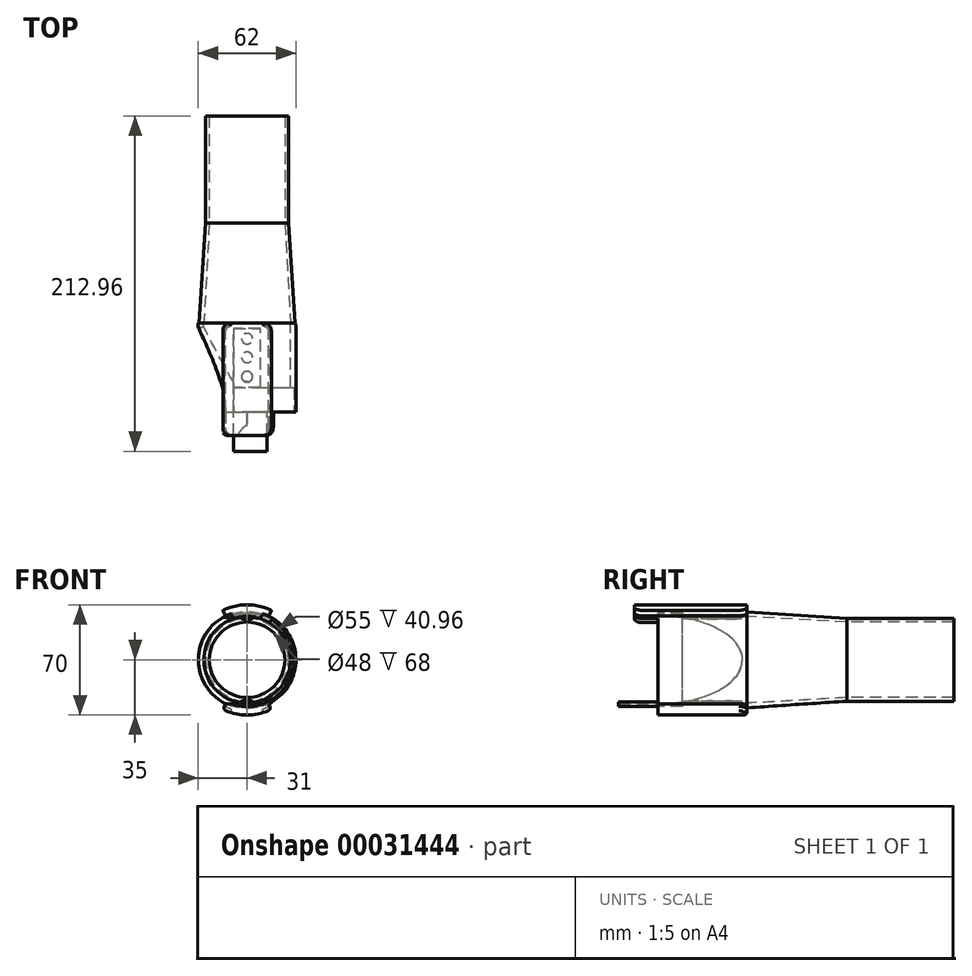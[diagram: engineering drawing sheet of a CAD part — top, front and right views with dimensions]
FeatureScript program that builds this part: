
annotation { "Feature Type Name" : "Feature", "Feature Type Description" : "" }
export const myFeature = defineFeature(function(context is Context, id is Id, definition is map)
    precondition{}
    {
        {
            var Q0;
            Q0=qCreatedBy(makeId("Front.planeOp"),FACE);
            var sketch = newSketch(context, id + "F0", { "sketchPlane" : qUnion([Q0])});
            skCircle(sketch, "E0", {"center": v(0, 0) * mm, "radius": 26.25 * mm});
            skSolve(sketch);
        }
        {
            var Q0;
            Q0=makeQuery(id+"F0.imprint","IMPRINT",FACE,{"disambiguationData":[TD([[makeQuery(id+"F0.imprint","IMPRINT",EDGE,{"derivedFrom":sQuery(id+"F0.wireOp",EDGE,"E0")}),1.0]])]});
            cPlane(context, id + "F1", {"entities" : qUnion([Q0]), "cplaneType" : CPlaneType.OFFSET, "offset" : 63.5 * mm, "width" : 150 * mm, "height" : 150 * mm});
        }
        {
            var Q0;
            Q0=qCreatedBy(id+"F1.planeOp",FACE);
            var sketch = newSketch(context, id + "F2", { "sketchPlane" : qUnion([Q0])});
            skCircle(sketch, "E1.0", {"center": v(0, 0) * mm, "radius": 26.25 * mm, "construction": true});
            skCircle(sketch, "E2", {"center": v(0, 0) * mm, "radius": 30.5 * mm});
            skSolve(sketch);
        }
        {
            var Q0;
            Q0=makeQuery(id+"F0.imprint","IMPRINT",FACE,{"disambiguationData":[TD([[makeQuery(id+"F0.imprint","IMPRINT",EDGE,{"derivedFrom":sQuery(id+"F0.wireOp",EDGE,"E0")}),1.0]])]});
            var Q1;
            Q1=makeQuery(id+"F2.imprint","IMPRINT",FACE,{"disambiguationData":[TD([[makeQuery(id+"F2.imprint","IMPRINT",EDGE,{"derivedFrom":sQuery(id+"F2.wireOp",EDGE,"E2")}),1.0]])]});
            loft(context, id + "F3", {"sheetProfilesArray" : [{ "sheetProfileEntities" : qUnion([Q0]) }, { "sheetProfileEntities" : qUnion([Q1]) }]});
        }
        {
            var Q0;
            Q0=makeQuery(id+"F3.opLoft","CAP_FACE",FACE,{"disambiguationData":[OSD([makeQuery(id+"F2.imprint","IMPRINT",FACE,{"disambiguationData":[TD([[makeQuery(id+"F2.imprint","IMPRINT",EDGE,{"derivedFrom":sQuery(id+"F2.wireOp",EDGE,"E2")}),1.0]])]})])],"isStart":true});
            var sketch = newSketch(context, id + "F4", { "sketchPlane" : qUnion([Q0])});
            skCircle(sketch, "E3.0", {"center": v(0, 0) * mm, "radius": 30.5 * mm, "construction": true});
            skCircle(sketch, "E4.0", {"center": v(0, 0) * mm, "radius": 27.5 * mm});
            skSolve(sketch);
        }
        {
            var Q0;
            Q0=makeQuery(id+"F3.opLoft","CAP_FACE",FACE,{"disambiguationData":[OSD([makeQuery(id+"F0.imprint","IMPRINT",FACE,{"disambiguationData":[TD([[makeQuery(id+"F0.imprint","IMPRINT",EDGE,{"derivedFrom":sQuery(id+"F0.wireOp",EDGE,"E0")}),1.0]])]})])],"isStart":true});
            var sketch = newSketch(context, id + "F5", { "sketchPlane" : qUnion([Q0])});
            skCircle(sketch, "E5.0", {"center": v(0, 0) * mm, "radius": 26.25 * mm, "construction": true});
            skCircle(sketch, "E6", {"center": v(0, 0) * mm, "radius": 24 * mm});
            skSolve(sketch);
        }
        {
            var Q1;
            Q1=makeQuery(id+"F5.imprint","IMPRINT",FACE,{"disambiguationData":[TD([[makeQuery(id+"F5.imprint","IMPRINT",EDGE,{"derivedFrom":sQuery(id+"F5.wireOp",EDGE,"E6")}),1.0]])]});
            var Q2;
            Q2=makeQuery(id+"F4.imprint","IMPRINT",FACE,{"disambiguationData":[TD([[makeQuery(id+"F4.imprint","IMPRINT",EDGE,{"derivedFrom":sQuery(id+"F4.wireOp",EDGE,"E4.0")}),1.0]])]});
            loft(context, id + "F6", {"operationType" : NewBodyOperationType.REMOVE, "sheetProfilesArray" : [{ "sheetProfileEntities" : qUnion([Q1]) }, { "sheetProfileEntities" : qUnion([Q2]) }]});
        }
        {
            var Q0;
            Q0=qCreatedBy(id+"F1.planeOp",FACE);
            var sketch = newSketch(context, id + "F7", { "sketchPlane" : qUnion([Q0])});
            skCircle(sketch, "E7", {"center": v(0, 0) * mm, "radius": 27.5 * mm});
            skCircle(sketch, "E8", {"center": v(0, 0) * mm, "radius": 31 * mm});
            skSolve(sketch);
        }
        {
            var Q0;
            Q0=makeQuery(id+"F7.imprint","IMPRINT",FACE,{"disambiguationData":[TD([[makeQuery(id+"F7.imprint","IMPRINT",EDGE,{"derivedFrom":sQuery(id+"F7.wireOp",EDGE,"E7")}),-1.0]])]});
            extrude(context, id + "F8", {"entities" : qUnion([Q0]), "operationType" : NewBodyOperationType.ADD, "depth" : 56.46 * mm});
        }
        {
            var Q0;
            Q0=makeQuery(id+"F8.opExtrude","CAP_FACE",FACE,{"disambiguationData":[OSD([sQuery(id+"F7.wireOp",EDGE,"E7"),sQuery(id+"F7.wireOp",EDGE,"E8")])],"isStart":false});
            var sketch = newSketch(context, id + "F9", { "sketchPlane" : qUnion([Q0])});
            skCircle(sketch, "E9.0", {"center": v(0, 0) * mm, "radius": 24 * mm, "construction": true});
            skLineSegment(sketch, "E10", {"start": v(-24, 0) * mm, "end": v(24, 0) * mm, "construction": true});
            skLineSegment(sketch, "E11", {"start": v(0, -24) * mm, "end": v(0, 24) * mm, "construction": true});
            skLineSegment(sketch, "E12.bottom", {"start": v(-8.5, 28.45) * mm, "end": v(8.5, 28.45) * mm});
            skLineSegment(sketch, "E12.top", {"start": v(-8.5, 25.33) * mm, "end": v(8.5, 25.33) * mm});
            skLineSegment(sketch, "E12.left", {"start": v(-8.5, 28.45) * mm, "end": v(-8.5, 25.33) * mm});
            skLineSegment(sketch, "E12.right", {"start": v(8.5, 28.45) * mm, "end": v(8.5, 25.33) * mm});
            skLineSegment(sketch, "E13", {"start": v(0, 28.45) * mm, "end": v(0, 25.33) * mm, "construction": true});
            skLineSegment(sketch, "E14.MirrorCS", {"start": v(-8.5, -25.33) * mm, "end": v(8.5, -25.33) * mm});
            skLineSegment(sketch, "E15.MirrorCS", {"start": v(8.5, -28.45) * mm, "end": v(8.5, -25.33) * mm});
            skLineSegment(sketch, "E16.MirrorCS", {"start": v(-8.5, -28.45) * mm, "end": v(8.5, -28.45) * mm});
            skLineSegment(sketch, "E17.MirrorCS", {"start": v(-8.5, -28.45) * mm, "end": v(-8.5, -25.33) * mm});
            skSolve(sketch);
        }
        {
            var Q0;
            Q0 = qSketchRegion(id + "F9", true);
            extrude(context, id + "F10", {"entities" : qUnion([Q0]), "operationType" : NewBodyOperationType.REMOVE, "oppositeDirection" : true, "depth" : 53 * mm});
        }
        {
            var Q0;
            Q0=makeQuery(id+"F8.opExtrude","CAP_FACE",FACE,{"disambiguationData":[OSD([sQuery(id+"F7.wireOp",EDGE,"c9ccfde4-7208-4a26-a400-e2db2dca37ce.0"),sQuery(id+"F7.wireOp",EDGE,"E7")])],"isStart":false});
            var sketch = newSketch(context, id + "F11", { "sketchPlane" : qUnion([Q0])});
            skArc(sketch, "E18", {"start": v(-8.5, -28.45) * mm, "mid": v(29.7, 0) * mm, "end": v(-8.5, 28.45) * mm});
            skArc(sketch, "E19", {"start": v(-8.5, -25.26) * mm, "mid": v(26.66, 0) * mm, "end": v(-8.5, 25.26) * mm});
            skLineSegment(sketch, "E20", {"start": v(-8.5, -28.45) * mm, "end": v(-8.5, -25.26) * mm});
            skLineSegment(sketch, "E21", {"start": v(-8.5, 28.45) * mm, "end": v(-8.5, 25.26) * mm});
            skSolve(sketch);
        }
        {
            var Q0;
            Q0=qSketchRegion(id+"F11",true);
            extrude(context, id + "F12", {"entities" : qUnion([Q0]), "operationType" : NewBodyOperationType.REMOVE, "oppositeDirection" : true, "depth" : 15.5 * mm});
        }
        {
            var Q0;
            Q0=makeQuery(id+"F10.boolean.opBoolean","COPY",FACE,{"derivedFrom":makeQuery(id+"F10.opExtrude","SWEPT_FACE",FACE,{"disambiguationData":[OSD([sQuery(id+"F9.wireOp",EDGE,"E16.MirrorCS")])]})});
            var sketch = newSketch(context, id + "F13", { "sketchPlane" : qUnion([Q0])});
            skCircle(sketch, "E22", {"center": v(0, -97.61) * mm, "radius": 3.45 * mm});
            skCircle(sketch, "E23", {"center": v(0, -85.3) * mm, "radius": 3.45 * mm});
            skCircle(sketch, "E24", {"center": v(0, -73.46) * mm, "radius": 3.45 * mm});
            skSolve(sketch);
        }
        {
            var Q0;
            Q0=makeQuery(id+"F10.boolean.opBoolean","COPY",FACE,{"derivedFrom":makeQuery(id+"F10.opExtrude","SWEPT_FACE",FACE,{"disambiguationData":[OSD([sQuery(id+"F9.wireOp",EDGE,"E12.bottom")])]})});
            var sketch = newSketch(context, id + "F14", { "sketchPlane" : qUnion([Q0])});
            skCircle(sketch, "E25", {"center": v(0, 97.61) * mm, "radius": 3.45 * mm});
            skPoint(sketch, "E25.centerSnap0", {"position": v(0, 104.46) * mm});
            skCircle(sketch, "E26", {"center": v(0, 85.3) * mm, "radius": 3.45 * mm});
            skCircle(sketch, "E27", {"center": v(0, 73.46) * mm, "radius": 3.45 * mm});
            skSolve(sketch);
        }
        {
            var Q0;
            Q0=qCreatedBy(makeId("Front.planeOp"),FACE);
            var sketch = newSketch(context, id + "F15", { "sketchPlane" : qUnion([Q0])});
            skCircle(sketch, "E28.0", {"center": v(0, 0) * mm, "radius": 26.25 * mm});
            skSolve(sketch);
        }
        {
            var Q0;
            Q0=qSketchRegion(id+"F14",true);
            extrude(context, id + "F16", {"entities" : qUnion([Q0]), "operationType" : NewBodyOperationType.ADD, "depth" : 2.5 * mm});
        }
        {
            var Q0;
            Q0=qSketchRegion(id+"F13",true);
            extrude(context, id + "F17", {"entities" : qUnion([Q0]), "operationType" : NewBodyOperationType.ADD, "depth" : 2.5 * mm});
        }
        {
            var Q0;
            Q0=makeQuery(id+"Fq4cvRqc1J3ZEHZ_1.boolean.opBoolean","MERGE",FACE,{"derivedFrom":[makeQuery(id+"F8.opExtrude","CAP_FACE",FACE,{"disambiguationData":[OSD([sQuery(id+"F7.wireOp",EDGE,"E7"),sQuery(id+"F7.wireOp",EDGE,"E8")])],"isStart":false}),makeQuery(id+"Fq4cvRqc1J3ZEHZ_1.opExtrude","CAP_FACE",FACE,{"disambiguationData":[OSD([sQuery(id+"FumwX2OVE5Degs5_1.wireOp",EDGE,"17daf398-062c-4251-8fa0-32e418a5fb52"),sQuery(id+"FumwX2OVE5Degs5_1.wireOp",EDGE,"bc219d95-7f0c-488f-9120-7b345b026efc")])],"isStart":true})]});
            var sketch = newSketch(context, id + "F18", { "sketchPlane" : qUnion([Q0])});
            skPoint(sketch, "E29.orphan", {"position": v(-8.5, -26.15) * mm});
            skPoint(sketch, "E30.orphan", {"position": v(8.5, -26.15) * mm});
            skArc(sketch, "E31.0", {"start": v(16.64, 26.15) * mm, "mid": v(0, 31) * mm, "end": v(-16.64, 26.15) * mm});
            skArc(sketch, "E32.0", {"start": v(-8.5, 26.15) * mm, "mid": v(-11.34, 25.05) * mm, "end": v(-14.03, 23.65) * mm});
            skArc(sketch, "E33.0", {"start": v(8.5, 26.15) * mm, "mid": v(0, 27.5) * mm, "end": v(-8.5, 26.15) * mm});
            skArc(sketch, "E34.0", {"start": v(14.03, 23.65) * mm, "mid": v(11.34, 25.05) * mm, "end": v(8.5, 26.15) * mm});
            skLineSegment(sketch, "E35", {"start": v(-14.03, 23.65) * mm, "end": v(-16.64, 26.15) * mm});
            skLineSegment(sketch, "E36.MirrorCS", {"start": v(14.03, 23.65) * mm, "end": v(16.64, 26.15) * mm});
            skSolve(sketch);
        }
        {
            var Q0;
            Q0 = qSketchRegion(id + "F18", true);
            extrude(context, id + "F19", {"entities" : qUnion([Q0]), "operationType" : NewBodyOperationType.ADD, "depth" : 15 * mm});
        }
        {
            var Q0;
            Q0=makeQuery(id+"F19.opExtrude","CAP_EDGE",EDGE,{"disambiguationData":[OSD([sQuery(id+"F18.wireOp",EDGE,"E35")])],"isStart":false});
            var Q1;
            Q1=makeQuery(id+"F19.opExtrude","CAP_EDGE",EDGE,{"disambiguationData":[OSD([sQuery(id+"F18.wireOp",EDGE,"E36.MirrorCS")])],"isStart":false});
            fillet(context, id + "F20", {"entities" : qUnion([Q0, Q1]), "radius" : 5 * mm, "tangentPropagation" : true, "allowEdgeOverflow" : false});
        }
        {
            var Q0;
            Q0=makeQuery(id+"F15.imprint","IMPRINT",FACE,{"disambiguationData":[TD([[makeQuery(id+"F15.imprint","IMPRINT",EDGE,{"derivedFrom":sQuery(id+"F15.wireOp",EDGE,"E28.0")}),1.0]])]});
            var sketch = newSketch(context, id + "F21", { "sketchPlane" : qUnion([Q0])});
            skCircle(sketch, "E37.0", {"center": v(0, 0) * mm, "radius": 26.25 * mm});
            skCircle(sketch, "E38.0", {"center": v(0, 0) * mm, "radius": 24 * mm});
            skSolve(sketch);
        }
        {
            var Q0;
            Q0 = qSketchRegion(id + "F21", true);
            extrude(context, id + "F22", {"entities" : qUnion([Q0]), "operationType" : NewBodyOperationType.ADD, "oppositeDirection" : true, "depth" : 68 * mm});
        }
        {
            var Q0;
            Q0=makeQuery(id+"F8.opExtrude","CAP_FACE",FACE,{"disambiguationData":[OSD([sQuery(id+"F7.wireOp",EDGE,"E7"),sQuery(id+"F7.wireOp",EDGE,"E8")])],"isStart":false});
            var sketch = newSketch(context, id + "F23", { "sketchPlane" : qUnion([Q0])});
            skArc(sketch, "E39.0", {"start": v(-13.55, -27.88) * mm, "mid": v(0, -31) * mm, "end": v(13.55, -27.88) * mm});
            skArc(sketch, "E40.0", {"start": v(-15.42, -31.42) * mm, "mid": v(0, -35) * mm, "end": v(15.42, -31.42) * mm});
            skLineSegment(sketch, "E41", {"start": v(15.42, -31.42) * mm, "end": v(13.55, -27.88) * mm});
            skLineSegment(sketch, "E42", {"start": v(0, 0) * mm, "end": v(0, -36.84) * mm, "construction": true});
            skLineSegment(sketch, "E43.MirrorCS", {"start": v(-15.42, -31.42) * mm, "end": v(-13.55, -27.88) * mm});
            skPoint(sketch, "E44.orphan", {"position": v(16.64, 26.15) * mm});
            skPoint(sketch, "E45.orphan", {"position": v(-16.64, 26.15) * mm});
            skSolve(sketch);
        }
        {
            var Q0;
            Q0 = qSketchRegion(id + "F23", true);
            extrude(context, id + "F24", {"entities" : qUnion([Q0]), "oppositeDirection" : true, "depth" : 56.46 * mm});
        }
        {
            var Q0;
            Q0=makeQuery(id+"F24.opExtrude","CAP_EDGE",EDGE,{"disambiguationData":[OSD([sQuery(id+"F23.wireOp",EDGE,"E43.MirrorCS")])],"isStart":false});
            var Q1;
            Q1=makeQuery(id+"F24.opExtrude","CAP_EDGE",EDGE,{"disambiguationData":[OSD([sQuery(id+"F23.wireOp",EDGE,"E41")])],"isStart":false});
            fillet(context, id + "F25", {"entities" : qUnion([Q0, Q1]), "radius" : 5 * mm, "tangentPropagation" : true, "allowEdgeOverflow" : false});
        }
        {
            var Q0;
            Q0=makeQuery(id+"F24.opExtrude","SWEPT_BODY",BODY,{"disambiguationData":[OSD([sQuery(id+"F23.wireOp",EDGE,"E39.0"),sQuery(id+"F23.wireOp",EDGE,"E40.0"),sQuery(id+"F23.wireOp",EDGE,"E41"),sQuery(id+"F23.wireOp",EDGE,"E43.MirrorCS")])]});
            var Q1;
            Q1=qCreatedBy(makeId("Top.planeOp"),FACE);
            mirror(context, id + "F26", {"operationType" : NewBodyOperationType.ADD, "entities" : qUnion([Q0]), "mirrorPlane" : qUnion([Q1])});
        }
        {
            var Q0;
            Q0=makeQuery(id+"F26.opPattern","COPY",FACE,{"derivedFrom":makeQuery(id+"F24.opExtrude","CAP_FACE",FACE,{"disambiguationData":[OSD([sQuery(id+"F23.wireOp",EDGE,"E39.0"),sQuery(id+"F23.wireOp",EDGE,"E40.0"),sQuery(id+"F23.wireOp",EDGE,"E41"),sQuery(id+"F23.wireOp",EDGE,"E43.MirrorCS")])],"isStart":true}),"instanceName":"1"});
            var sketch = newSketch(context, id + "F27", { "sketchPlane" : qUnion([Q0])});
            skLineSegment(sketch, "E46.0.0", {"start": v(-15.42, 31.42) * mm, "end": v(-13.55, 27.88) * mm});
            skArc(sketch, "E46.0.1", {"start": v(-13.55, 27.88) * mm, "mid": v(0, 31) * mm, "end": v(13.55, 27.88) * mm});
            skLineSegment(sketch, "E46.0.2", {"start": v(13.55, 27.88) * mm, "end": v(15.42, 31.42) * mm});
            skArc(sketch, "E46.0.3", {"start": v(15.42, 31.42) * mm, "mid": v(0, 35) * mm, "end": v(-15.42, 31.42) * mm});
            skSolve(sketch);
        }
        {
            var Q0;
            Q0 = qSketchRegion(id + "F27", true);
            var Q1;
            Q1=makeQuery(id+"F19.opExtrude","CAP_FACE",FACE,{"disambiguationData":[OSD([sQuery(id+"F18.wireOp",EDGE,"E31.0"),sQuery(id+"F18.wireOp",EDGE,"E32.0"),sQuery(id+"F18.wireOp",EDGE,"E33.0"),sQuery(id+"F18.wireOp",EDGE,"E34.0"),sQuery(id+"F18.wireOp",EDGE,"E35"),sQuery(id+"F18.wireOp",EDGE,"E36.MirrorCS")])],"isStart":false});
            extrude(context, id + "F28", {"entities" : qUnion([Q0]), "operationType" : NewBodyOperationType.ADD, "endBound" : BoundingType.UP_TO_SURFACE, "endBoundEntityFace" : qUnion([Q1]), "depth" : 25 * mm});
        }
        {
            var Q0;
            Q0=makeQuery(id+"F28.opExtrude","TWEAK_EDGE",EDGE,{"derivedFrom":[makeQuery(id+"F19.opExtrude","CAP_FACE",FACE,{"disambiguationData":[OSD([sQuery(id+"F18.wireOp",EDGE,"E31.0"),sQuery(id+"F18.wireOp",EDGE,"E32.0"),sQuery(id+"F18.wireOp",EDGE,"E33.0"),sQuery(id+"F18.wireOp",EDGE,"E34.0"),sQuery(id+"F18.wireOp",EDGE,"E35"),sQuery(id+"F18.wireOp",EDGE,"E36.MirrorCS")])],"isStart":false}),makeQuery(id+"F27.imprint","IMPRINT",EDGE,{"derivedFrom":sQuery(id+"F27.wireOp",EDGE,"E46.0.0")})]});
            var Q1;
            Q1=makeQuery(id+"F28.opExtrude","TWEAK_EDGE",EDGE,{"derivedFrom":[makeQuery(id+"F19.opExtrude","CAP_FACE",FACE,{"disambiguationData":[OSD([sQuery(id+"F18.wireOp",EDGE,"E31.0"),sQuery(id+"F18.wireOp",EDGE,"E32.0"),sQuery(id+"F18.wireOp",EDGE,"E33.0"),sQuery(id+"F18.wireOp",EDGE,"E34.0"),sQuery(id+"F18.wireOp",EDGE,"E35"),sQuery(id+"F18.wireOp",EDGE,"E36.MirrorCS")])],"isStart":false}),makeQuery(id+"F27.imprint","IMPRINT",EDGE,{"derivedFrom":sQuery(id+"F27.wireOp",EDGE,"E46.0.2")})]});
            fillet(context, id + "F29", {"entities" : qUnion([Q0, Q1]), "radius" : 5 * mm, "tangentPropagation" : true, "allowEdgeOverflow" : false});
        }
        {
            var Q0;
            {var subQ0=sQuery(id+"F7.wireOp",EDGE,"E8");var subQ1=sQuery(id+"F23.wireOp",EDGE,"E41");var subQ2=makeQuery(id+"F25.opFillet","BLEND_FACE",FACE,{"disambiguationData":[OSD([subQ1])]});Q0=makeQuery(id+"F26.boolean.opBoolean","SPLIT",EDGE,{"disambiguationData":[TD([subQ2])],"derivedFrom":makeQuery(id+"F8.opExtrude","CAP_EDGE",EDGE,{"disambiguationData":[OSD([subQ0])],"isStart":true})});}
            fillet(context, id + "F30", {"entities" : qUnion([Q0]), "radius" : 5 * mm, "tangentPropagation" : true, "allowEdgeOverflow" : false});
        }
        {
            var Q0;
            Q0=qCreatedBy(makeId("Right.planeOp"),FACE);
            var sketch = newSketch(context, id + "F31", { "sketchPlane" : qUnion([Q0])});
            skFitSpline(sketch, "E47.0.0", {"points": [v(-129.96, 26.36) * mm, v(-130.36, 26.36) * mm, v(-130.75, 26.38) * mm, v(-131.14, 26.43) * mm, v(-131.53, 26.48) * mm, v(-131.9, 26.55) * mm, v(-132.26, 26.65) * mm, v(-132.61, 26.74) * mm, v(-132.94, 26.86) * mm, v(-133.24, 27) * mm, v(-133.54, 27.12) * mm, v(-133.8, 27.26) * mm, v(-134.03, 27.42) * mm, v(-134.26, 27.57) * mm, v(-134.45, 27.73) * mm, v(-134.6, 27.9) * mm, v(-134.74, 28.05) * mm, v(-134.84, 28.22) * mm, v(-134.9, 28.38) * mm, v(-134.96, 28.54) * mm, v(-134.97, 28.7) * mm, v(-134.95, 28.84) * mm, v(-134.92, 28.98) * mm, v(-134.85, 29.12) * mm, v(-134.73, 29.25) * mm], "construction": true});
            skFitSpline(sketch, "E47.0.1", {"points": [v(-134.73, 29.25) * mm, v(-134.57, 29.08) * mm, v(-134.34, 28.9) * mm, v(-134.04, 28.75) * mm, v(-133.72, 28.58) * mm, v(-133.36, 28.43) * mm, v(-132.94, 28.3) * mm, v(-132.5, 28.17) * mm, v(-132.03, 28.07) * mm, v(-131.53, 28) * mm, v(-131.02, 27.92) * mm, v(-130.5, 27.88) * mm, v(-129.96, 27.88) * mm], "construction": true});
            skLineSegment(sketch, "E47.0.2", {"start": v(-129.96, 27.88) * mm, "end": v(-68.5, 27.88) * mm, "construction": true});
            skFitSpline(sketch, "E47.0.3", {"points": [v(-68.5, 27.88) * mm, v(-67.84, 27.88) * mm, v(-67.2, 27.94) * mm, v(-66.57, 28.05) * mm, v(-66.27, 28.1) * mm, v(-65.98, 28.17) * mm, v(-65.7, 28.25) * mm, v(-65.43, 28.33) * mm, v(-65.18, 28.41) * mm, v(-64.94, 28.5) * mm, v(-64.71, 28.6) * mm, v(-64.5, 28.7) * mm, v(-64.32, 28.8) * mm, v(-64.15, 28.9) * mm, v(-64, 29) * mm, v(-63.87, 29.11) * mm, v(-63.75, 29.22) * mm, v(-63.66, 29.32) * mm, v(-63.6, 29.43) * mm, v(-63.53, 29.53) * mm, v(-63.5, 29.63) * mm, v(-63.5, 29.72) * mm], "construction": true});
            skLineSegment(sketch, "E47.0.4", {"start": v(-63.5, -29.7) * mm, "end": v(-63.5, 29.7) * mm, "construction": true});
            skFitSpline(sketch, "E47.0.5", {"points": [v(-63.5, -29.72) * mm, v(-63.5, -29.63) * mm, v(-63.53, -29.53) * mm, v(-63.6, -29.43) * mm, v(-63.65, -29.32) * mm, v(-63.75, -29.22) * mm, v(-63.87, -29.11) * mm, v(-64, -29) * mm, v(-64.14, -28.9) * mm, v(-64.32, -28.8) * mm, v(-64.5, -28.7) * mm, v(-64.71, -28.6) * mm, v(-64.94, -28.5) * mm, v(-65.18, -28.41) * mm, v(-65.43, -28.33) * mm, v(-65.7, -28.25) * mm, v(-65.97, -28.17) * mm, v(-66.26, -28.1) * mm, v(-66.57, -28.05) * mm, v(-67.2, -27.94) * mm, v(-67.84, -27.88) * mm, v(-68.5, -27.88) * mm], "construction": true});
            skLineSegment(sketch, "E47.0.6", {"start": v(-68.5, -27.88) * mm, "end": v(-119.96, -27.88) * mm, "construction": true});
            skLineSegment(sketch, "E47.0.7", {"start": v(-119.96, 26.15) * mm, "end": v(-119.96, -27.88) * mm, "construction": true});
            skLineSegment(sketch, "E47.0.8", {"start": v(-119.96, 26.15) * mm, "end": v(-129.96, 26.15) * mm, "construction": true});
            skEllipse(sketch, "E48", {"center": v(-119.96, 0) * mm, "majorRadius": 27.88 * mm, "minorRadius": 53.66 * mm, "majorAxis": v(0, -1)});
            skSolve(sketch);
        }
        {
            var Q0;
            Q0 = qSketchRegion(id + "F31", true);
            extrude(context, id + "F32", {"entities" : qUnion([Q0]), "operationType" : NewBodyOperationType.REMOVE, "oppositeDirection" : true, "depth" : 38.12 * mm});
        }
        {
            var Q0;
            Q0=makeQuery(id+"F24.opExtrude","SWEPT_EDGE",EDGE,{"disambiguationData":[OSD([sQuery(id+"F23.wireOp",EDGE,"E40.0"),sQuery(id+"F23.wireOp",EDGE,"E43.MirrorCS")])]});
            fillet(context, id + "F33", {"entities" : qUnion([Q0]), "radius" : 2 * mm, "tangentPropagation" : true, "allowEdgeOverflow" : false});
        }
        {
            var Q0;
            Q0=makeQuery(id+"F26.boolean.opBoolean","MERGE",FACE,{"derivedFrom":[makeQuery(id+"F8.opExtrude","CAP_FACE",FACE,{"disambiguationData":[OSD([sQuery(id+"F7.wireOp",EDGE,"E7"),sQuery(id+"F7.wireOp",EDGE,"E8")])],"isStart":false}),makeQuery(id+"F24.opExtrude","CAP_FACE",FACE,{"disambiguationData":[OSD([sQuery(id+"F23.wireOp",EDGE,"E39.0"),sQuery(id+"F23.wireOp",EDGE,"E40.0"),sQuery(id+"F23.wireOp",EDGE,"E41"),sQuery(id+"F23.wireOp",EDGE,"E43.MirrorCS")])],"isStart":true})]});
            var sketch = newSketch(context, id + "F34", { "sketchPlane" : qUnion([Q0])});
            skLineSegment(sketch, "E49", {"start": v(13.55, -27.88) * mm, "end": v(12.78, -26.8) * mm});
            skLineSegment(sketch, "E50.0", {"start": v(14.42, -29.54) * mm, "end": v(13.55, -27.88) * mm});
            skArc(sketch, "E51.0", {"start": v(13.43, -32.32) * mm, "mid": v(14.54, -31.15) * mm, "end": v(14.42, -29.54) * mm});
            skArc(sketch, "E52.0", {"start": v(-13.43, -32.32) * mm, "mid": v(0, -35) * mm, "end": v(13.43, -32.32) * mm});
            skArc(sketch, "E53.0", {"start": v(-14.42, -29.54) * mm, "mid": v(-14.54, -31.15) * mm, "end": v(-13.43, -32.32) * mm});
            skLineSegment(sketch, "E54.0", {"start": v(-14.42, -29.54) * mm, "end": v(-13.55, -27.88) * mm});
            skLineSegment(sketch, "E55.0", {"start": v(-13.55, -27.88) * mm, "end": v(-8.5, -27.88) * mm});
            skLineSegment(sketch, "E56.0", {"start": v(-8.5, -28.45) * mm, "end": v(-8.5, -27.88) * mm});
            skArc(sketch, "E57.0", {"start": v(-8.5, -28.45) * mm, "mid": v(27.07, -12.2) * mm, "end": v(15.67, 25.22) * mm});
            skSolve(sketch);
        }
        {
            var Q0;
            {var subQ1=sQuery(id+"F34.wireOp",EDGE,"E49");Q0=makeQuery(id+"F34.imprint","IMPRINT",FACE,{"disambiguationData":[TD([[makeQuery(id+"F34.imprint","IMPRINT",EDGE,{"derivedFrom":subQ1}),1.0]])]});}
            extrude(context, id + "F35", {"entities" : qUnion([Q0]), "operationType" : NewBodyOperationType.ADD, "depth" : 25 * mm});
        }
    });
